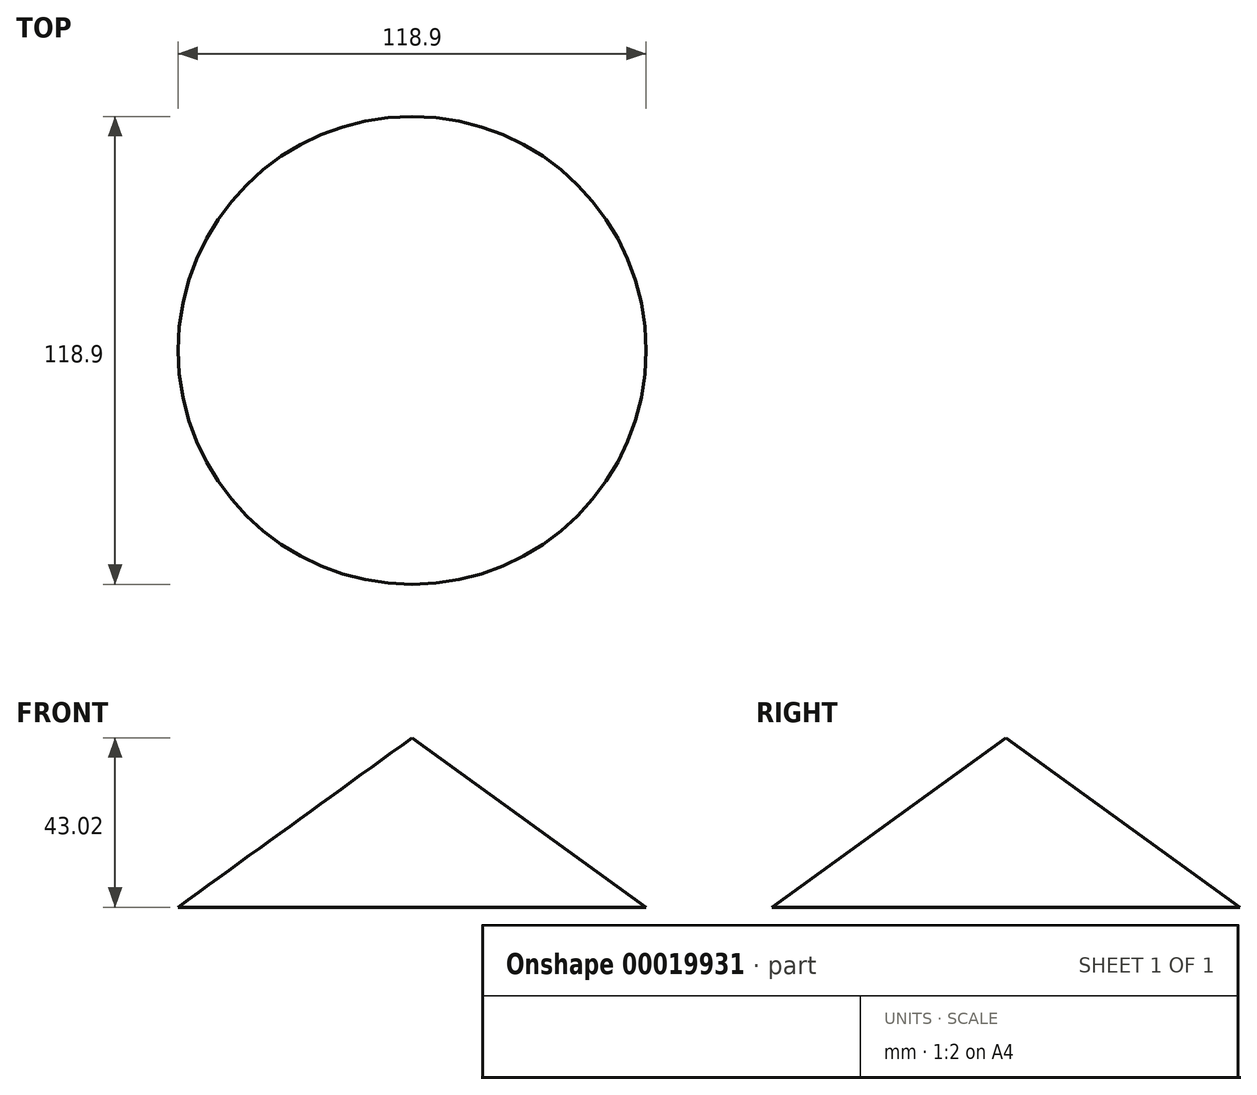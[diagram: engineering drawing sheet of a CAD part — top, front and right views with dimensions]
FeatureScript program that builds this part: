
annotation { "Feature Type Name" : "Feature", "Feature Type Description" : "" }
export const myFeature = defineFeature(function(context is Context, id is Id, definition is map)
    precondition{}
    {
        {
            var Q0;
            Q0=qCreatedBy(makeId("Front.planeOp"),FACE);
            var sketch = newSketch(context, id + "F0", { "sketchPlane" : qUnion([Q0])});
            skLineSegment(sketch, "E0", {"start": v(0, 0) * mm, "end": v(0, 43.02) * mm});
            skLineSegment(sketch, "E1", {"start": v(0, 43.02) * mm, "end": v(59.45, 0) * mm});
            skLineSegment(sketch, "E2", {"start": v(59.45, 0) * mm, "end": v(0, 0) * mm});
            skSolve(sketch);
        }
        {
            var Q0;
            Q0=makeQuery(id+"F0.imprint","IMPRINT",FACE,{"disambiguationData":[TD([[makeQuery(id+"F0.imprint","IMPRINT",EDGE,{"derivedFrom":sQuery(id+"F0.wireOp",EDGE,"E0")}),-1.0]])]});
            var Q1;
            Q1=sQuery(id+"F0.wireOp",EDGE,"E0");
            revolve(context, id + "F1", {"entities" : qUnion([Q0]), "axis" : qUnion([Q1]), "revolveType" : RevolveType.FULL});
        }
    });
